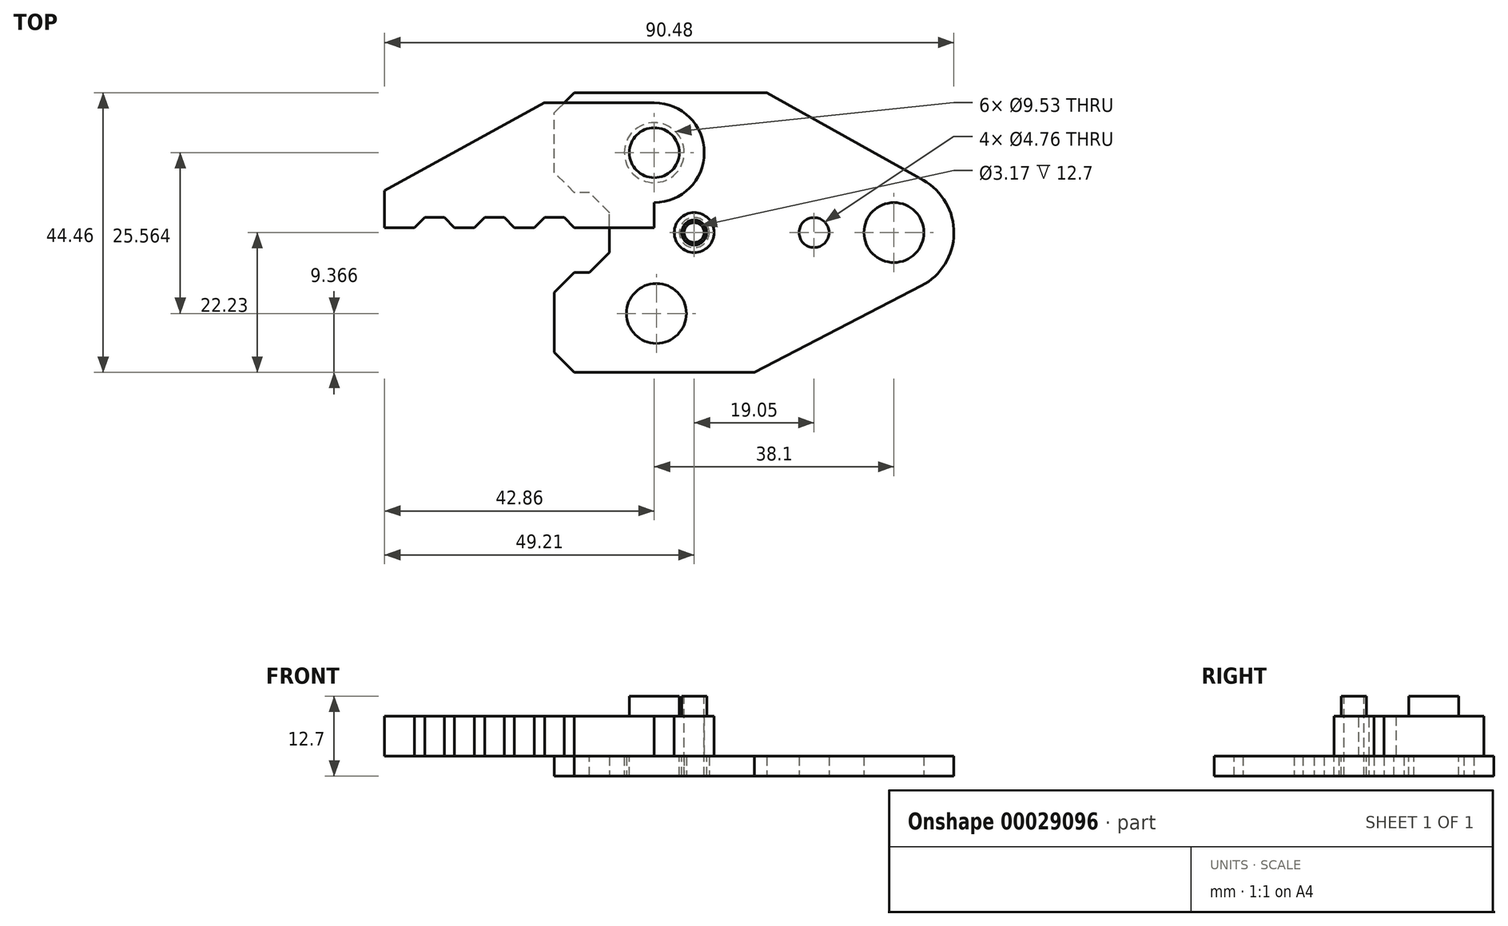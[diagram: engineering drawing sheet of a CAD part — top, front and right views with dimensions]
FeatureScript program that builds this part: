
annotation { "Feature Type Name" : "Feature", "Feature Type Description" : "" }
export const myFeature = defineFeature(function(context is Context, id is Id, definition is map)
    precondition{}
    {
        {
            var Q0;
            Q0=qCreatedBy(makeId("Top.planeOp"),FACE);
            var sketch = newSketch(context, id + "F0", { "sketchPlane" : qUnion([Q0])});
            skCircle(sketch, "E0", {"center": v(0, 0) * mm, "radius": 4.76 * mm});
            skLineSegment(sketch, "E1", {"start": v(0, 0) * mm, "end": v(-38.1, 0) * mm, "construction": true});
            skLineSegment(sketch, "E2", {"start": v(-38.1, 12.7) * mm, "end": v(-38.1, -12.7) * mm, "construction": true});
            skCircle(sketch, "E3", {"center": v(-38.1, 12.7) * mm, "radius": 4.76 * mm});
            skCircle(sketch, "E4", {"center": v(-37.77, -12.86) * mm, "radius": 4.76 * mm});
            skArc(sketch, "E5", {"start": v(4.38, -8.46) * mm, "mid": v(9.52, -0.15) * mm, "end": v(4.65, 8.31) * mm});
            skLineSegment(sketch, "E6", {"start": v(-45.23, -6.35) * mm, "end": v(-45.23, 6.35) * mm});
            skLineSegment(sketch, "E7", {"start": v(-45.23, 6.35) * mm, "end": v(-53.98, 6.35) * mm});
            skLineSegment(sketch, "E8", {"start": v(-53.98, 6.35) * mm, "end": v(-53.98, 22.23) * mm});
            skLineSegment(sketch, "E9", {"start": v(-53.98, 22.23) * mm, "end": v(-20.22, 22.22) * mm});
            skLineSegment(sketch, "E10", {"start": v(-20.22, 22.22) * mm, "end": v(4.65, 8.31) * mm});
            skLineSegment(sketch, "E11", {"start": v(-45.23, -6.35) * mm, "end": v(-53.98, -6.35) * mm});
            skLineSegment(sketch, "E12", {"start": v(-53.98, -6.35) * mm, "end": v(-53.98, -22.23) * mm});
            skLineSegment(sketch, "E13", {"start": v(-53.98, -22.23) * mm, "end": v(-22.18, -22.22) * mm});
            skLineSegment(sketch, "E14", {"start": v(-22.18, -22.23) * mm, "end": v(4.38, -8.46) * mm});
            skCircle(sketch, "E15", {"center": v(-12.7, 0) * mm, "radius": 2.38 * mm});
            skCircle(sketch, "E16", {"center": v(-31.75, 0) * mm, "radius": 2.38 * mm});
            skSolve(sketch);
        }
        {
            var Q0;
            Q0=makeQuery(id+"F0.imprint","IMPRINT",FACE,{"disambiguationData":[TD([[makeQuery(id+"F0.imprint","IMPRINT",EDGE,{"derivedFrom":sQuery(id+"F0.wireOp",EDGE,"E0")}),-1.0]])]});
            extrude(context, id + "F1", {"entities" : qUnion([Q0]), "depth" : 3.17 * mm});
        }
        {
            var Q0;
            Q0=makeQuery(id+"F1.opExtrude","SWEPT_EDGE",EDGE,{"disambiguationData":[OSD([sQuery(id+"F0.wireOp",EDGE,"E6"),sQuery(id+"F0.wireOp",EDGE,"E7")])]});
            var Q1;
            Q1=makeQuery(id+"F1.opExtrude","SWEPT_EDGE",EDGE,{"disambiguationData":[OSD([sQuery(id+"F0.wireOp",EDGE,"E7"),sQuery(id+"F0.wireOp",EDGE,"E8")])]});
            var Q2;
            Q2=makeQuery(id+"F1.opExtrude","SWEPT_EDGE",EDGE,{"disambiguationData":[OSD([sQuery(id+"F0.wireOp",EDGE,"E6"),sQuery(id+"F0.wireOp",EDGE,"E11")])]});
            var Q3;
            Q3=makeQuery(id+"F1.opExtrude","SWEPT_EDGE",EDGE,{"disambiguationData":[OSD([sQuery(id+"F0.wireOp",EDGE,"E11"),sQuery(id+"F0.wireOp",EDGE,"E12")])]});
            var Q4;
            Q4=makeQuery(id+"F1.opExtrude","SWEPT_EDGE",EDGE,{"disambiguationData":[OSD([sQuery(id+"F0.wireOp",EDGE,"E12"),sQuery(id+"F0.wireOp",EDGE,"E13")])]});
            var Q5;
            Q5=makeQuery(id+"F1.opExtrude","SWEPT_EDGE",EDGE,{"disambiguationData":[OSD([sQuery(id+"F0.wireOp",EDGE,"E8"),sQuery(id+"F0.wireOp",EDGE,"E9")])]});
            chamfer(context, id + "F2", {"entities" : qUnion([Q0, Q1, Q2, Q3, Q4, Q5]), "width" : 3.17 * mm, "tangentPropagation" : true});
        }
        {
            var Q0;
            Q0=makeQuery(id+"F1.opExtrude","CAP_FACE",FACE,{"disambiguationData":[OSD([sQuery(id+"F0.wireOp",EDGE,"E0"),sQuery(id+"F0.wireOp",EDGE,"E3"),sQuery(id+"F0.wireOp",EDGE,"E4"),sQuery(id+"F0.wireOp",EDGE,"E5"),sQuery(id+"F0.wireOp",EDGE,"E6"),sQuery(id+"F0.wireOp",EDGE,"E7"),sQuery(id+"F0.wireOp",EDGE,"E8"),sQuery(id+"F0.wireOp",EDGE,"E9"),sQuery(id+"F0.wireOp",EDGE,"E10"),sQuery(id+"F0.wireOp",EDGE,"E11"),sQuery(id+"F0.wireOp",EDGE,"E12"),sQuery(id+"F0.wireOp",EDGE,"E13"),sQuery(id+"F0.wireOp",EDGE,"E14")])],"isStart":false});
            var sketch = newSketch(context, id + "F3", { "sketchPlane" : qUnion([Q0])});
            skArc(sketch, "E17", {"start": v(-38.1, 4.76) * mm, "mid": v(-30.16, 12.7) * mm, "end": v(-38.1, 20.64) * mm});
            skLineSegment(sketch, "E18", {"start": v(-38.1, 4.76) * mm, "end": v(-38.1, 0.8) * mm});
            skLineSegment(sketch, "E19", {"start": v(-38.1, 0.8) * mm, "end": v(-80.96, 0.8) * mm});
            skLineSegment(sketch, "E20", {"start": v(-80.96, 0.8) * mm, "end": v(-80.96, 6.68) * mm});
            skLineSegment(sketch, "E21", {"start": v(-80.96, 6.68) * mm, "end": v(-55.56, 20.64) * mm});
            skLineSegment(sketch, "E22", {"start": v(-55.56, 20.64) * mm, "end": v(-38.1, 20.64) * mm});
            skSolve(sketch);
        }
        {
            var Q0;
            Q0=makeQuery(id+"F3.imprint","IMPRINT",FACE,{"disambiguationData":[TD([[makeQuery(id+"F3.imprint","IMPRINT",EDGE,{"derivedFrom":sQuery(id+"F3.wireOp",EDGE,"E17")}),1.0]])]});
            var Q1;
            {var subQ14=sQuery(id+"F3.wireOp",EDGE,"E20");Q1=makeQuery(id+"F3.imprint","IMPRINT",FACE,{"disambiguationData":[TD([[makeQuery(id+"F3.imprint","IMPRINT",EDGE,{"derivedFrom":subQ14}),-1.0]])]});}
            var Q2;
            Q2=makeQuery(id+"F3.imprint","IMPRINT",FACE,{"disambiguationData":[TD([[makeQuery(id+"F3.imprint","IMPRINT",EDGE,{"derivedFrom":makeQuery(id+"F1.opExtrude","CAP_EDGE",EDGE,{"disambiguationData":[OSD([sQuery(id+"F0.wireOp",EDGE,"E3")])],"isStart":false})}),1.0]])]});
            extrude(context, id + "F4", {"entities" : qUnion([Q0, Q1, Q2]), "depth" : 6.35 * mm});
        }
        {
            var Q0;
            Q0=makeQuery(id+"F4.opExtrude","CAP_FACE",FACE,{"disambiguationData":[OSD([sQuery(id+"F3.wireOp",EDGE,"E17"),sQuery(id+"F3.wireOp",EDGE,"E18"),sQuery(id+"F3.wireOp",EDGE,"E19"),sQuery(id+"F3.wireOp",EDGE,"E20"),sQuery(id+"F3.wireOp",EDGE,"E21"),sQuery(id+"F3.wireOp",EDGE,"E22")])],"isStart":false});
            var sketch = newSketch(context, id + "F5", { "sketchPlane" : qUnion([Q0])});
            skCircle(sketch, "E23", {"center": v(-38.1, 12.7) * mm, "radius": 3.97 * mm});
            skSolve(sketch);
        }
        {
            var Q0;
            Q0=makeQuery(id+"F5.imprint","IMPRINT",FACE,{"disambiguationData":[TD([[makeQuery(id+"F5.imprint","IMPRINT",EDGE,{"derivedFrom":sQuery(id+"F5.wireOp",EDGE,"E23")}),1.0]])]});
            extrude(context, id + "F6", {"entities" : qUnion([Q0]), "operationType" : NewBodyOperationType.ADD, "depth" : 3.17 * mm});
        }
        {
            var Q0;
            Q0=makeQuery(id+"F4.opExtrude","CAP_FACE",FACE,{"disambiguationData":[OSD([sQuery(id+"F3.wireOp",EDGE,"E17"),sQuery(id+"F3.wireOp",EDGE,"E18"),sQuery(id+"F3.wireOp",EDGE,"E19"),sQuery(id+"F3.wireOp",EDGE,"E20"),sQuery(id+"F3.wireOp",EDGE,"E21"),sQuery(id+"F3.wireOp",EDGE,"E22")])],"isStart":true});
            var sketch = newSketch(context, id + "F7", { "sketchPlane" : qUnion([Q0])});
            skCircle(sketch, "E24", {"center": v(-38.1, -12.7) * mm, "radius": 3.97 * mm});
            skSolve(sketch);
        }
        {
            var Q0;
            Q0=makeQuery(id+"F7.imprint","IMPRINT",FACE,{"disambiguationData":[TD([[makeQuery(id+"F7.imprint","IMPRINT",EDGE,{"derivedFrom":sQuery(id+"F7.wireOp",EDGE,"E24")}),1.0]])]});
            extrude(context, id + "F8", {"entities" : qUnion([Q0]), "operationType" : NewBodyOperationType.ADD, "depth" : 3.17 * mm});
        }
        {
            var Q0;
            Q0=makeQuery(id+"F4.opExtrude","CAP_FACE",FACE,{"disambiguationData":[OSD([sQuery(id+"F3.wireOp",EDGE,"E17"),sQuery(id+"F3.wireOp",EDGE,"E18"),sQuery(id+"F3.wireOp",EDGE,"E19"),sQuery(id+"F3.wireOp",EDGE,"E20"),sQuery(id+"F3.wireOp",EDGE,"E21"),sQuery(id+"F3.wireOp",EDGE,"E22")])],"isStart":false});
            var sketch = newSketch(context, id + "F9", { "sketchPlane" : qUnion([Q0])});
            skLineSegment(sketch, "E25", {"start": v(-76.2, 0.8) * mm, "end": v(-74.56, 2.43) * mm});
            skLineSegment(sketch, "E26", {"start": v(-74.56, 2.43) * mm, "end": v(-71.49, 2.43) * mm});
            skLineSegment(sketch, "E27", {"start": v(-71.49, 2.43) * mm, "end": v(-69.85, 0.8) * mm});
            skLineSegment(sketch, "E28", {"start": v(-76.2, 0.8) * mm, "end": v(-69.85, 0.8) * mm});
            skLineSegment(sketch, "E29.1.0.0", {"start": v(-65.04, 2.43) * mm, "end": v(-61.96, 2.43) * mm});
            skLineSegment(sketch, "E29.1.0.1", {"start": v(-66.67, 0.8) * mm, "end": v(-60.32, 0.8) * mm});
            skLineSegment(sketch, "E29.1.0.2", {"start": v(-61.96, 2.43) * mm, "end": v(-60.32, 0.8) * mm});
            skLineSegment(sketch, "E29.1.0.3", {"start": v(-66.67, 0.8) * mm, "end": v(-65.04, 2.43) * mm});
            skLineSegment(sketch, "E29.2.0.0", {"start": v(-55.51, 2.43) * mm, "end": v(-52.44, 2.43) * mm});
            skLineSegment(sketch, "E29.2.0.1", {"start": v(-57.15, 0.8) * mm, "end": v(-50.8, 0.8) * mm});
            skLineSegment(sketch, "E29.2.0.2", {"start": v(-52.44, 2.43) * mm, "end": v(-50.8, 0.8) * mm});
            skLineSegment(sketch, "E29.2.0.3", {"start": v(-57.15, 0.8) * mm, "end": v(-55.51, 2.43) * mm});
            skLineSegment(sketch, "E29.direction1", {"start": v(-74.56, 2.43) * mm, "end": v(-65.04, 2.43) * mm, "construction": true});
            skSolve(sketch);
        }
        {
            var Q0;
            Q0 = qSketchRegion(id + "F9", true);
            extrude(context, id + "F10", {"entities" : qUnion([Q0]), "operationType" : NewBodyOperationType.REMOVE, "oppositeDirection" : true, "depth" : 25.4 * mm});
        }
        {
            var Q0;
            Q0=makeQuery(id+"F1.opExtrude","CAP_FACE",FACE,{"disambiguationData":[OSD([sQuery(id+"F0.wireOp",EDGE,"E0"),sQuery(id+"F0.wireOp",EDGE,"E3"),sQuery(id+"F0.wireOp",EDGE,"E4"),sQuery(id+"F0.wireOp",EDGE,"E5"),sQuery(id+"F0.wireOp",EDGE,"E6"),sQuery(id+"F0.wireOp",EDGE,"E7"),sQuery(id+"F0.wireOp",EDGE,"E8"),sQuery(id+"F0.wireOp",EDGE,"E9"),sQuery(id+"F0.wireOp",EDGE,"E10"),sQuery(id+"F0.wireOp",EDGE,"E11"),sQuery(id+"F0.wireOp",EDGE,"E12"),sQuery(id+"F0.wireOp",EDGE,"E13"),sQuery(id+"F0.wireOp",EDGE,"E14"),sQuery(id+"F0.wireOp",EDGE,"E15"),sQuery(id+"F0.wireOp",EDGE,"E16")])],"isStart":false});
            var sketch = newSketch(context, id + "F11", { "sketchPlane" : qUnion([Q0])});
            skCircle(sketch, "E30", {"center": v(-31.75, 0) * mm, "radius": 3.18 * mm});
            skSolve(sketch);
        }
        {
            var Q0;
            Q0 = qSketchRegion(id + "F11", true);
            extrude(context, id + "F12", {"entities" : qUnion([Q0]), "depth" : 6.35 * mm});
        }
        {
            var Q0;
            Q0=makeQuery(id+"F12.opExtrude","CAP_FACE",FACE,{"disambiguationData":[OSD([sQuery(id+"F11.wireOp",EDGE,"E30")])],"isStart":false});
            var sketch = newSketch(context, id + "F13", { "sketchPlane" : qUnion([Q0])});
            skCircle(sketch, "E31", {"center": v(-31.75, 0) * mm, "radius": 1.98 * mm});
            skSolve(sketch);
        }
        {
            var Q0;
            Q0 = qSketchRegion(id + "F13", true);
            extrude(context, id + "F14", {"entities" : qUnion([Q0]), "operationType" : NewBodyOperationType.ADD, "depth" : 3.17 * mm});
        }
        {
            var Q0;
            Q0=makeQuery(id+"F12.opExtrude","CAP_FACE",FACE,{"disambiguationData":[OSD([sQuery(id+"F11.wireOp",EDGE,"E30")])],"isStart":true});
            var sketch = newSketch(context, id + "F15", { "sketchPlane" : qUnion([Q0])});
            skCircle(sketch, "E32", {"center": v(-31.75, 0) * mm, "radius": 1.98 * mm});
            skSolve(sketch);
        }
        {
            var Q0;
            Q0 = qSketchRegion(id + "F15", true);
            extrude(context, id + "F16", {"entities" : qUnion([Q0]), "operationType" : NewBodyOperationType.ADD, "depth" : 3.17 * mm});
        }
        {
            var Q0;
            Q0=makeQuery(id+"F14.opExtrude","CAP_FACE",FACE,{"disambiguationData":[OSD([sQuery(id+"F13.wireOp",EDGE,"E31")])],"isStart":false});
            var sketch = newSketch(context, id + "F17", { "sketchPlane" : qUnion([Q0])});
            skCircle(sketch, "E33", {"center": v(-31.75, 0) * mm, "radius": 1.59 * mm});
            skSolve(sketch);
        }
        {
            var Q0;
            Q0=makeQuery(id+"F17.imprint","IMPRINT",FACE,{"disambiguationData":[TD([[makeQuery(id+"F17.imprint","IMPRINT",EDGE,{"derivedFrom":sQuery(id+"F17.wireOp",EDGE,"E33")}),1.0]])]});
            extrude(context, id + "F18", {"entities" : qUnion([Q0]), "operationType" : NewBodyOperationType.REMOVE, "endBound" : BoundingType.THROUGH_ALL, "oppositeDirection" : true, "depth" : 25.4 * mm});
        }
    });
